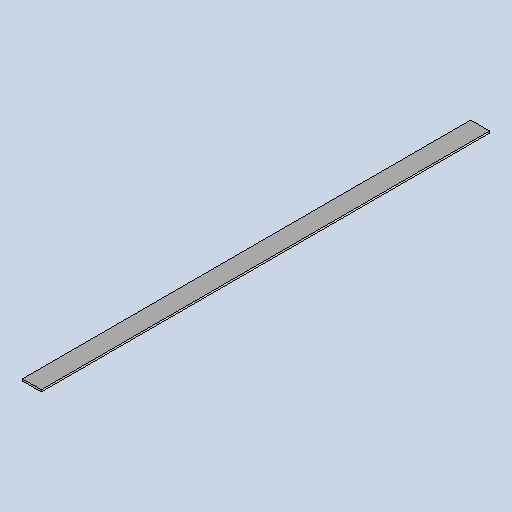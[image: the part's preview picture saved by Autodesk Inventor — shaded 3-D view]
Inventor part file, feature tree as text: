
AUTODESK INVENTOR PART (.ipt)
format: ipt  version: 2025.3 (Build 293356030, 356C)  size: 149,504 bytes
history: native  units: mm
features: other x2, sheet_metal_op x1, sketch x1
ambient origin geometry x8: Origin, YZ Plane, XZ Plane, XY Plane, X Axis, Y Axis, Z Axis, Center Point
bodies: Solid1 (feature_tree)
feature tree (4):
  sheet_metal_op  "Face1"
  sketch  "Sketch1"  dims[d2=20.0mm d3=2.0mm d18=475.0mm]
  other  "Plate1"
  other  "Definition1"
